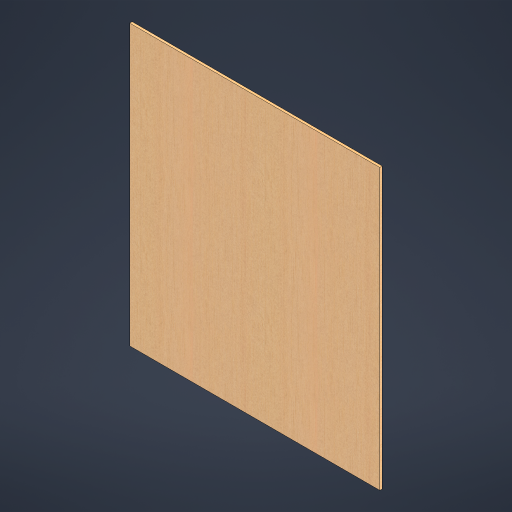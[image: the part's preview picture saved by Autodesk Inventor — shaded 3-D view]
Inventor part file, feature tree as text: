
AUTODESK INVENTOR PART (.ipt)
format: ipt  version: 2024 (Build 280153000, 153)  size: 314,880 bytes
history: native  units: mm
features: other x2, extrude x1, sketch x1
ambient origin geometry x8: Origin, YZ Plane, XZ Plane, XY Plane, X Axis, Y Axis, Z Axis, Center Point
bodies: Body1 (feature_tree)
feature tree (4):
  other  "솔리드1"
  extrude  "돌출1"  Depth=510.0mm
  sketch  "스케치1"
  other  "Finish1"
